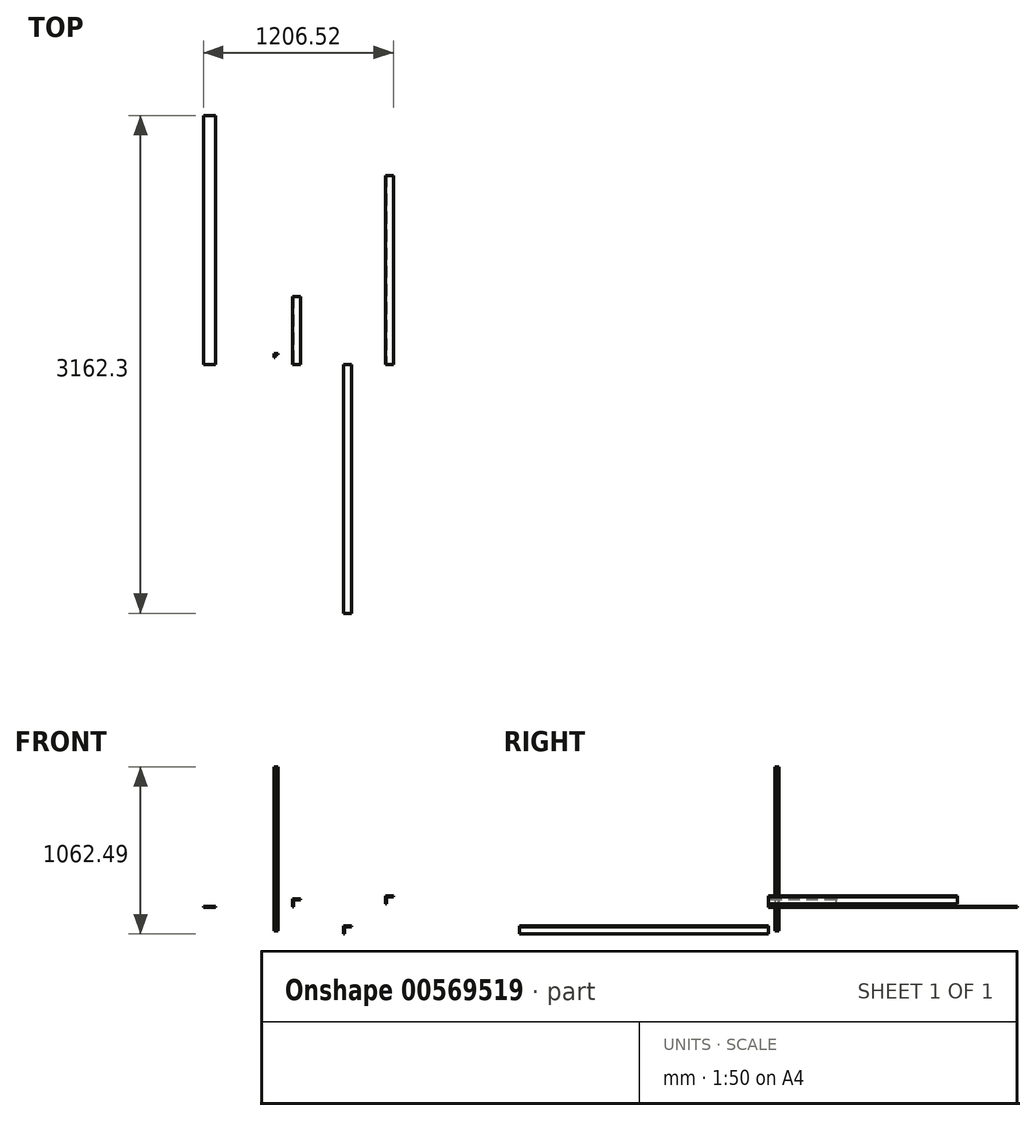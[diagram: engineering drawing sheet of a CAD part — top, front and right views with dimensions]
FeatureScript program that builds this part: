
annotation { "Feature Type Name" : "Feature", "Feature Type Description" : "" }
export const myFeature = defineFeature(function(context is Context, id is Id, definition is map)
    precondition{}
    {
        {
            var Q0;
            Q0=qCreatedBy(makeId("Front.planeOp"),FACE);
            var sketch = newSketch(context, id + "F0", { "sketchPlane" : qUnion([Q0])});
            skLineSegment(sketch, "E0.bottom", {"start": v(-7.25, -21.1) * mm, "end": v(-0.9, -21.1) * mm});
            skLineSegment(sketch, "E0.top", {"start": v(-7.25, 29.7) * mm, "end": v(-0.9, 29.7) * mm});
            skLineSegment(sketch, "E0.left", {"start": v(-7.25, -21.1) * mm, "end": v(-7.25, 29.7) * mm});
            skLineSegment(sketch, "E0.right", {"start": v(-0.9, -21.1) * mm, "end": v(-0.9, 29.7) * mm});
            skLineSegment(sketch, "E1.bottom", {"start": v(-0.9, 29.7) * mm, "end": v(43.55, 29.7) * mm});
            skLineSegment(sketch, "E1.top", {"start": v(-0.9, 23.36) * mm, "end": v(43.55, 23.36) * mm});
            skLineSegment(sketch, "E1.left", {"start": v(-0.9, 29.7) * mm, "end": v(-0.9, 23.36) * mm});
            skLineSegment(sketch, "E1.right", {"start": v(43.55, 29.7) * mm, "end": v(43.55, 23.36) * mm});
            skSolve(sketch);
        }
        {
            var Q0;
            Q0=makeQuery(id+"F0.imprint","IMPRINT",FACE,{"disambiguationData":[TD([[makeQuery(id+"F0.imprint","IMPRINT",EDGE,{"derivedFrom":sQuery(id+"F0.wireOp",EDGE,"E0.bottom")}),1.0]])]});
            var Q1;
            Q1=makeQuery(id+"F0.imprint","IMPRINT",FACE,{"disambiguationData":[TD([[makeQuery(id+"F0.imprint","IMPRINT",EDGE,{"derivedFrom":sQuery(id+"F0.wireOp",EDGE,"E1.bottom")}),-1.0]])]});
            extrude(context, id + "F1", {"entities" : qUnion([Q0, Q1]), "depth" : 1581.15 * mm, "offsetDistance" : 25.4 * mm});
        }
        {
            var Q0;
            Q0=qCreatedBy(makeId("Top.planeOp"),FACE);
            var sketch = newSketch(context, id + "F2", { "sketchPlane" : qUnion([Q0])});
            skLineSegment(sketch, "E2.bottom", {"start": v(-447.61, 68.48) * mm, "end": v(-441.26, 68.48) * mm});
            skLineSegment(sketch, "E2.top", {"start": v(-447.61, 43.08) * mm, "end": v(-441.26, 43.08) * mm});
            skLineSegment(sketch, "E2.left", {"start": v(-447.61, 68.48) * mm, "end": v(-447.61, 43.08) * mm});
            skLineSegment(sketch, "E2.right", {"start": v(-441.26, 68.48) * mm, "end": v(-441.26, 43.08) * mm});
            skLineSegment(sketch, "E3.bottom", {"start": v(-441.26, 68.48) * mm, "end": v(-422.21, 68.48) * mm});
            skLineSegment(sketch, "E3.top", {"start": v(-441.26, 62.13) * mm, "end": v(-422.21, 62.13) * mm});
            skLineSegment(sketch, "E3.left", {"start": v(-441.26, 68.48) * mm, "end": v(-441.26, 62.13) * mm});
            skLineSegment(sketch, "E3.right", {"start": v(-422.21, 68.48) * mm, "end": v(-422.21, 62.13) * mm});
            skSolve(sketch);
        }
        {
            var Q0;
            Q0=makeQuery(id+"F2.imprint","IMPRINT",FACE,{"disambiguationData":[TD([[makeQuery(id+"F2.imprint","IMPRINT",EDGE,{"derivedFrom":sQuery(id+"F2.wireOp",EDGE,"E3.bottom")}),-1.0]])]});
            var Q1;
            Q1=makeQuery(id+"F2.imprint","IMPRINT",FACE,{"disambiguationData":[TD([[makeQuery(id+"F2.imprint","IMPRINT",EDGE,{"derivedFrom":sQuery(id+"F2.wireOp",EDGE,"E2.bottom")}),-1.0]])]});
            extrude(context, id + "F3", {"entities" : qUnion([Q0, Q1]), "depth" : 1041.4 * mm, "offsetDistance" : 25.4 * mm});
        }
        {
            var Q0;
            Q0=qCreatedBy(makeId("Front.planeOp"),FACE);
            var sketch = newSketch(context, id + "F4", { "sketchPlane" : qUnion([Q0])});
            skLineSegment(sketch, "E4.bottom", {"start": v(-331.94, 151.24) * mm, "end": v(-325.6, 151.24) * mm});
            skLineSegment(sketch, "E4.top", {"start": v(-331.94, 202.04) * mm, "end": v(-325.6, 202.04) * mm});
            skLineSegment(sketch, "E4.left", {"start": v(-331.94, 151.24) * mm, "end": v(-331.94, 202.04) * mm});
            skLineSegment(sketch, "E4.right", {"start": v(-325.6, 151.24) * mm, "end": v(-325.6, 202.04) * mm});
            skLineSegment(sketch, "E5.bottom", {"start": v(-325.6, 202.04) * mm, "end": v(-281.14, 202.04) * mm});
            skLineSegment(sketch, "E5.top", {"start": v(-325.6, 195.69) * mm, "end": v(-281.14, 195.69) * mm});
            skLineSegment(sketch, "E5.left", {"start": v(-325.6, 202.04) * mm, "end": v(-325.6, 195.69) * mm});
            skLineSegment(sketch, "E5.right", {"start": v(-281.14, 202.04) * mm, "end": v(-281.14, 195.69) * mm});
            skSolve(sketch);
        }
        {
            var Q0;
            Q0=makeQuery(id+"F4.imprint","IMPRINT",FACE,{"disambiguationData":[TD([[makeQuery(id+"F4.imprint","IMPRINT",EDGE,{"derivedFrom":sQuery(id+"F4.wireOp",EDGE,"E5.bottom")}),-1.0]])]});
            var Q1;
            Q1=makeQuery(id+"F4.imprint","IMPRINT",FACE,{"disambiguationData":[TD([[makeQuery(id+"F4.imprint","IMPRINT",EDGE,{"derivedFrom":sQuery(id+"F4.wireOp",EDGE,"E4.bottom")}),1.0]])]});
            extrude(context, id + "F5", {"entities" : qUnion([Q0, Q1]), "oppositeDirection" : true, "depth" : 431.8 * mm, "offsetDistance" : 25.4 * mm});
        }
        {
            var Q0;
            Q0=qCreatedBy(makeId("Front.planeOp"),FACE);
            var sketch = newSketch(context, id + "F6", { "sketchPlane" : qUnion([Q0])});
            skLineSegment(sketch, "E6.bottom", {"start": v(258.12, 171.22) * mm, "end": v(264.47, 171.22) * mm});
            skLineSegment(sketch, "E6.top", {"start": v(258.12, 222.02) * mm, "end": v(264.47, 222.02) * mm});
            skLineSegment(sketch, "E6.left", {"start": v(258.12, 171.22) * mm, "end": v(258.12, 222.02) * mm});
            skLineSegment(sketch, "E6.right", {"start": v(264.47, 171.22) * mm, "end": v(264.47, 222.02) * mm});
            skLineSegment(sketch, "E7.bottom", {"start": v(264.47, 222.02) * mm, "end": v(308.92, 222.02) * mm});
            skLineSegment(sketch, "E7.top", {"start": v(264.47, 215.67) * mm, "end": v(308.92, 215.67) * mm});
            skLineSegment(sketch, "E7.left", {"start": v(264.47, 222.02) * mm, "end": v(264.47, 215.67) * mm});
            skLineSegment(sketch, "E7.right", {"start": v(308.92, 222.02) * mm, "end": v(308.92, 215.67) * mm});
            skSolve(sketch);
        }
        {
            var Q0;
            Q0=makeQuery(id+"F6.imprint","IMPRINT",FACE,{"disambiguationData":[TD([[makeQuery(id+"F6.imprint","IMPRINT",EDGE,{"derivedFrom":sQuery(id+"F6.wireOp",EDGE,"E6.bottom")}),1.0]])]});
            var Q1;
            Q1=makeQuery(id+"F6.imprint","IMPRINT",FACE,{"disambiguationData":[TD([[makeQuery(id+"F6.imprint","IMPRINT",EDGE,{"derivedFrom":sQuery(id+"F6.wireOp",EDGE,"E7.bottom")}),-1.0]])]});
            extrude(context, id + "F7", {"entities" : qUnion([Q0, Q1]), "oppositeDirection" : true, "depth" : 1200.15 * mm, "offsetDistance" : 25.4 * mm});
        }
        {
            var Q0;
            Q0=qCreatedBy(makeId("Front.planeOp"),FACE);
            var sketch = newSketch(context, id + "F8", { "sketchPlane" : qUnion([Q0])});
            skLineSegment(sketch, "E8.bottom", {"start": v(-897.6, 156.07) * mm, "end": v(-821.4, 156.07) * mm});
            skLineSegment(sketch, "E8.top", {"start": v(-897.6, 149.72) * mm, "end": v(-821.4, 149.72) * mm});
            skLineSegment(sketch, "E8.left", {"start": v(-897.6, 156.07) * mm, "end": v(-897.6, 149.72) * mm});
            skLineSegment(sketch, "E8.right", {"start": v(-821.4, 156.07) * mm, "end": v(-821.4, 149.72) * mm});
            skLineSegment(sketch, "E9.bottom", {"start": v(-897.6, 149.72) * mm, "end": v(-891.25, 149.72) * mm});
            skLineSegment(sketch, "E9.top", {"start": v(-897.6, 117.97) * mm, "end": v(-891.25, 117.97) * mm});
            skLineSegment(sketch, "E9.left", {"start": v(-897.6, 149.72) * mm, "end": v(-897.6, 117.97) * mm});
            skLineSegment(sketch, "E9.right", {"start": v(-891.25, 149.72) * mm, "end": v(-891.25, 117.97) * mm});
            skLineSegment(sketch, "E10.bottom", {"start": v(-821.4, 149.72) * mm, "end": v(-827.75, 149.72) * mm});
            skLineSegment(sketch, "E10.top", {"start": v(-821.4, 117.97) * mm, "end": v(-827.75, 117.97) * mm});
            skLineSegment(sketch, "E10.left", {"start": v(-821.4, 149.72) * mm, "end": v(-821.4, 117.97) * mm});
            skLineSegment(sketch, "E10.right", {"start": v(-827.75, 149.72) * mm, "end": v(-827.75, 117.97) * mm});
            skSolve(sketch);
        }
        {
            var Q0;
            Q0=makeQuery(id+"F8.imprint","IMPRINT",FACE,{"disambiguationData":[TD([[makeQuery(id+"F8.imprint","IMPRINT",EDGE,{"derivedFrom":sQuery(id+"F8.wireOp",EDGE,"E9.bottom")}),-1.0]])]});
            var Q1;
            Q1=makeQuery(id+"F8.imprint","IMPRINT",FACE,{"disambiguationData":[TD([[makeQuery(id+"F8.imprint","IMPRINT",EDGE,{"derivedFrom":sQuery(id+"F8.wireOp",EDGE,"E8.bottom")}),-1.0]])]});
            var Q2;
            Q2=makeQuery(id+"F8.imprint","IMPRINT",FACE,{"disambiguationData":[TD([[makeQuery(id+"F8.imprint","IMPRINT",EDGE,{"derivedFrom":sQuery(id+"F8.wireOp",EDGE,"E10.bottom")}),1.0]])]});
            extrude(context, id + "F9", {"entities" : qUnion([Q0, Q1, Q2]), "oppositeDirection" : true, "depth" : 1581.15 * mm, "offsetDistance" : 25.4 * mm});
        }
    });
